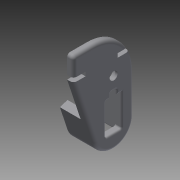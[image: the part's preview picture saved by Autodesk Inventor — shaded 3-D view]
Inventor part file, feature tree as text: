
AUTODESK INVENTOR PART (.ipt)
format: ipt  version: 2015 (Build 190159000, 159)  size: 507,392 bytes
history: native  units: mm
features: sketch x35, extrude x30, fillet x3
ambient origin geometry x8: Origin, YZ Plane, XZ Plane, XY Plane, X Axis, Y Axis, Z Axis, Center Point
bodies: Solid1 (feature_tree)
feature tree (68):
  extrude  "Extrusion1"  Depth=66.3mm
  extrude  "Extrusion2"  Depth=55.0mm
  extrude  "Extrusion3"  Depth=55.0mm
  extrude  "Extrusion4"  Depth=9.9mm
  extrude  "Extrusion5"  Depth=9.9mm
  extrude  "Extrusion6"  Depth=3.0mm
  extrude  "Extrusion7"  Depth=3.0mm
  extrude  "Extrusion8"  Depth=13.6mm
  extrude  "Extrusion9"  Depth=45.0mm
  sketch  "Sketch10"  dims[d22=15.0mm d23=5.0mm d24=0.0mm]
  extrude  "Extrusion10"  Depth=5.0mm TaperAngle=0.0deg
  extrude  "Extrusion11"  Depth=55.0mm
  extrude  "Extrusion12"  Depth=20.0mm
  sketch  "Sketch14"  dims[d33=10.0mm d34=32.9mm d35=0.0mm]
  extrude  "Extrusion13"  Depth=5.0mm TaperAngle=0.0deg
  extrude  "Extrusion14"  Depth=10.0mm TaperAngle=0.0deg
  extrude  "Extrusion15"  Depth=25.0mm
  extrude  "Extrusion16"  Depth=10.0mm TaperAngle=0.0deg
  extrude  "Extrusion17"  Depth=15.0mm
  sketch  "Sketch20"  dims[d50=28.0mm d51=5.0mm d52=0.0mm]
  extrude  "Extrusion18"  Depth=10.0mm
  extrude  "Extrusion19"  Depth=32.9mm TaperAngle=0.0deg
  extrude  "Extrusion20"  Depth=5.0mm TaperAngle=0.0deg
  extrude  "Extrusion21"  Depth=10.0mm
  extrude  "Extrusion22"  Depth=13.6mm
  extrude  "Extrusion23"  Depth=10.0mm
  sketch  "Sketch27"  dims[d68=21.4mm d69=2.0mm]
  extrude  "Extrusion24"  Depth=12.2mm
  extrude  "Extrusion25"  Depth=5.0mm TaperAngle=0.0deg
  extrude  "Extrusion26"  Depth=2.0mm
  sketch  "Sketch31"  dims[d81=2.0mm]
  extrude  "Extrusion27"  Depth=2.0mm
  extrude  "Extrusion28"  Depth=2.05mm
  extrude  "Extrusion29"  Depth=5.0mm TaperAngle=0.0deg
  extrude  "Extrusion30"  Depth=2.05mm
  fillet  "Fillet1"  Radius=2.0mm
  fillet  "Fillet2"  Radius=10.6mm
  fillet  "Fillet3"  Radius=2.05mm
  sketch  "Sketch1"  dims[d0=33.15mm d2=66.3mm]
  sketch  "Sketch2"  dims[d4=18.1mm d5=55.0mm]
  sketch  "Sketch3"  dims[d6=20.0mm d7=55.0mm]
  sketch  "Sketch4"  dims[d8=40.2mm d9=9.9mm]
  sketch  "Sketch5"  dims[d10=9.5mm d11=9.9mm]
  sketch  "Sketch6"  dims[d12=9.5mm d13=3.0mm]
  sketch  "Sketch7"  dims[d14=3.0mm d15=3.0mm]
  sketch  "Sketch8"  dims[d16=3.0mm d17=13.6mm]
  sketch  "Sketch9"  dims[d20=25.0mm d21=45.0mm]
  sketch  "Sketch11"  dims[d25=18.1mm d26=55.0mm]
  sketch  "Sketch12"  dims[d27=40.2mm d28=20.0mm]
  sketch  "Sketch13"  dims[d29=5.0mm d30=0.0mm d31=5.0mm d32=0.0mm]
  sketch  "Sketch15"  dims[d36=25.0mm d37=0.0mm d38=25.0mm]
  sketch  "Sketch16"  dims[d39=10.0mm d40=5.0mm d41=0.0mm]
  sketch  "Sketch17"  dims[d42=12.5mm d43=15.0mm]
  sketch  "Sketch18"  dims[d44=10.0mm d45=0.0mm d46=18.0mm]
  sketch  "Sketch19"  dims[d47=5.0mm d48=32.9mm d49=0.0mm]
  sketch  "Sketch21"  dims[d53=10.0mm d54=0.0mm d55=5.0mm]
  sketch  "Sketch22"  dims[d56=12.5mm d57=13.6mm]
  sketch  "Sketch23"  dims[d58=10.0mm d59=0.0mm d60=12.5mm]
  sketch  "Sketch24"  dims[d61=12.4mm d62=12.2mm]
  sketch  "Sketch25"  dims[d63=6.2mm d64=5.0mm d65=0.0mm]
  sketch  "Sketch26"  dims[d66=10.6mm d67=2.0mm]
  sketch  "Sketch28"  dims[d70=5.0mm d71=0.0mm d72=2.05mm]
  sketch  "Sketch29"  dims[d73=2.05mm d74=5.0mm d75=0.0mm]
  sketch  "Sketch30"  dims[d76=21.4mm d77=2.05mm d78=2.0mm d79=10.6mm d80=2.05mm]
  sketch  "Sketch32"  dims[d82=5.0mm d83=0.0mm]
  sketch  "Sketch33"  dims[d84=45.0mm]
  sketch  "Sketch34"  dims[d86=5.0mm]
  sketch  "Sketch35"  dims[d87=5.0mm d88=39.0mm d89=0.0mm d90=22.0mm d91=5.0mm d92=0.0mm d93=3.0mm d94=0.0mm d95=10.0mm d96=2.0mm d97=0.0mm d98=2.0mm d99=0.0mm d100=10.25mm d101=7.25mm d102=22.0mm d103=0.0mm d104=10.0mm d105=2.0mm d106=0.0mm d107=10.0mm d108=3.0mm d109=0.0mm d111=14.0mm d112=14.0mm d113=5.0mm d114=0.0mm d115=15.0mm d116=15.0mm d117=37.9mm d118=0.0mm d119=29.9mm d120=0.0mm d121=29.9mm d122=0.0mm d123=29.9mm d124=0.0mm d125=47.0mm d126=8.0mm d127=8.0mm d128=0.0mm d129=54.0mm d130=10.0mm d132=25.9mm d133=0.0mm d134=2.0mm d135=2.0mm d136=4.0mm]
